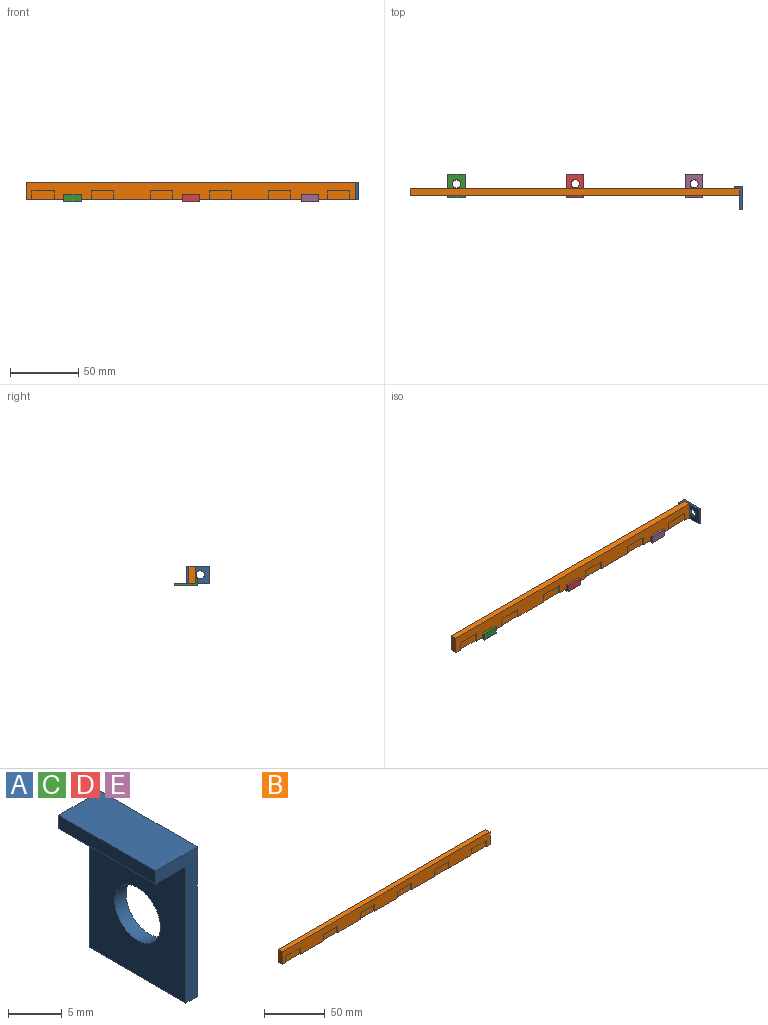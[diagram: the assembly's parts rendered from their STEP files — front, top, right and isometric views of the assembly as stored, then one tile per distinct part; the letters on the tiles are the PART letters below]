
ASSEMBLY  parts=5 mates=1
PART A: 9 faces, bbox 5.5x12.7x17 mm
  f0: plane 12.7x5.5mm, normal (0,0,1), area 69.8mm2, adj f1,f5,f6,f7
  f1: plane 12.7x1.5mm, normal (-1,0,0), area 19.1mm2, adj f0,f2,f6,f7
  f2: plane 12.7x4mm, normal (0,0,-1), area 50.8mm2, adj f1,f3,f6,f7
  f3: plane 15.5x12.7mm, normal (-1,0,0), area 168.6mm2, adj f2,f4,f6,f7,f8
  f4: plane 12.7x1.5mm, normal (0,0,-1), area 19mm2, adj f3,f5,f6,f7
  f5: plane 17x12.7mm, normal (1,0,0), area 187.6mm2, adj f0,f4,f6,f7,f8
  f6: plane 17x5.5mm, normal (0,-1,0), area 31.5mm2, adj f0,f1,f2,f3,f4,f5
  f7: plane 17x5.5mm, normal (0,1,0), area 31.5mm2, adj f0,f1,f2,f3,f4,f5
  f8: cylinder r=3mm len=6mm, axis (1,0,0), area 28.3mm2, adj f3,f5
PART B: 30 faces, bbox 241.3x4.8x12.7 mm
  f0: plane 16.44x6.35mm, normal (0,-1,0), area 104.4mm2, adj f5,f26,f27,f28
  f1: plane 16.44x6.35mm, normal (0,-1,0), area 104.4mm2, adj f5,f23,f24,f25
  f2: plane 16.44x6.35mm, normal (0,-1,0), area 104.4mm2, adj f5,f20,f21,f22
  f3: plane 16.44x6.35mm, normal (0,-1,0), area 104.4mm2, adj f5,f17,f18,f19
  f4: plane 16.44x6.35mm, normal (0,-1,0), area 104.4mm2, adj f5,f14,f15,f16
  f5: plane 241.3x4.75mm, normal (0,0,-1), area 1072.2mm2, adj f0,f1,f2,f3,f4,f6,f8,f9
  f6: plane 12.7x4.75mm, normal (1,0,0), area 60.3mm2, adj f5,f7,f10,f29
  f7: plane 241.3x4.75mm, normal (0,0,1), area 1146.2mm2, adj f6,f8,f10,f29
  f8: plane 12.7x4.75mm, normal (-1,0,0), area 60.3mm2, adj f5,f7,f10,f29
  f9: plane 16.44x6.35mm, normal (0,-1,0), area 104.4mm2, adj f5,f11,f12,f13
  f10: plane 241.3x12.7mm, normal (0,1,0), area 3064.5mm2, adj f5,f6,f7,f8
  f11: plane 6.35x0.75mm, normal (1,0,0), area 4.8mm2, adj f5,f9,f12,f29
  f12: plane 16.44x0.75mm, normal (0,0,-1), area 12.3mm2, adj f9,f11,f13,f29
  f13: plane 6.35x0.75mm, normal (-1,0,0), area 4.8mm2, adj f5,f9,f12,f29
  f14: plane 6.35x0.75mm, normal (1,0,0), area 4.8mm2, adj f4,f5,f15,f29
  f15: plane 16.44x0.75mm, normal (0,0,-1), area 12.3mm2, adj f4,f14,f16,f29
  f16: plane 6.35x0.75mm, normal (-1,0,0), area 4.8mm2, adj f4,f5,f15,f29
  f17: plane 6.35x0.75mm, normal (1,0,0), area 4.8mm2, adj f3,f5,f18,f29
  f18: plane 16.44x0.75mm, normal (0,0,-1), area 12.3mm2, adj f3,f17,f19,f29
  f19: plane 6.35x0.75mm, normal (-1,0,0), area 4.8mm2, adj f3,f5,f18,f29
  f20: plane 6.35x0.75mm, normal (1,0,0), area 4.8mm2, adj f2,f5,f21,f29
  f21: plane 16.44x0.75mm, normal (0,0,-1), area 12.3mm2, adj f2,f20,f22,f29
  f22: plane 6.35x0.75mm, normal (-1,0,0), area 4.8mm2, adj f2,f5,f21,f29
  f23: plane 6.35x0.75mm, normal (1,0,0), area 4.8mm2, adj f1,f5,f24,f29
  f24: plane 16.44x0.75mm, normal (0,0,-1), area 12.3mm2, adj f1,f23,f25,f29
  f25: plane 6.35x0.75mm, normal (-1,0,0), area 4.8mm2, adj f1,f5,f24,f29
  f26: plane 6.35x0.75mm, normal (1,0,0), area 4.8mm2, adj f0,f5,f27,f29
  f27: plane 16.44x0.75mm, normal (0,0,-1), area 12.3mm2, adj f0,f26,f28,f29
  f28: plane 6.35x0.75mm, normal (-1,0,0), area 4.8mm2, adj f0,f5,f27,f29
  f29: plane 241.3x12.7mm, normal (0,-1,0), area 2438.1mm2, adj f5,f6,f7,f8,f11,f12,f13,f14
PART C: same geometry as A
PART D: same geometry as A
PART E: same geometry as A
PLACE A rot(axis=(-1,0,0),90deg) t=(114.83,-2.48,23.09)mm
PLACE B t=(-16,13.74,23.19)mm
PLACE C rot(axis=(0.58,0.58,-0.58),120deg) t=(-102.63,25.43,6.36)mm
PLACE D rot(axis=(0.58,0.58,-0.58),120deg) t=(-15.88,25.5,6.39)mm
PLACE E rot(axis=(0.58,0.58,-0.58),120deg) t=(71.19,25.48,6.41)mm
MATE planar B.f6 <-> A.f3  axis (1,0,0) through (104.65,11.36,23.19)mm
